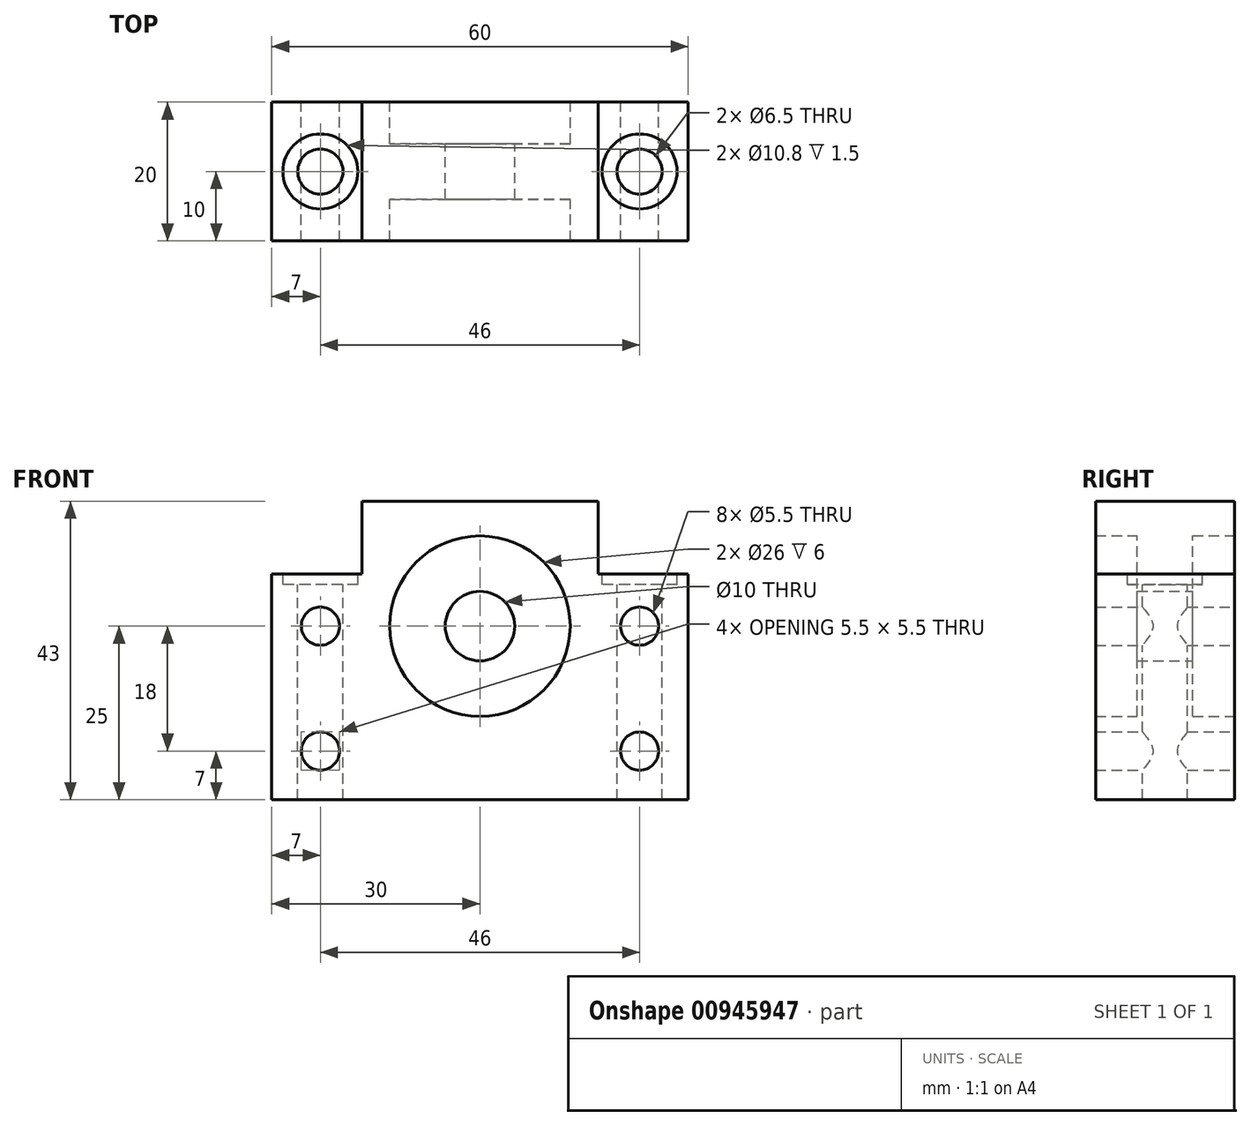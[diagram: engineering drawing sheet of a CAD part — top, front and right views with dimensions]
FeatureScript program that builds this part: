
annotation { "Feature Type Name" : "Feature", "Feature Type Description" : "" }
export const myFeature = defineFeature(function(context is Context, id is Id, definition is map)
    precondition{}
    {
        {
            var Q0;
            Q0=qCreatedBy(makeId("Front.planeOp"),FACE);
            var sketch = newSketch(context, id + "F0", { "sketchPlane" : qUnion([Q0])});
            skLineSegment(sketch, "E0.bottom", {"start": v(30, -16.25) * mm, "end": v(-30, -16.25) * mm});
            skLineSegment(sketch, "E0.top", {"start": v(30, 16.25) * mm, "end": v(17, 16.25) * mm});
            skLineSegment(sketch, "E0.left", {"start": v(30, -16.25) * mm, "end": v(30, 16.25) * mm});
            skLineSegment(sketch, "E0.right", {"start": v(-30, -16.25) * mm, "end": v(-30, 16.25) * mm});
            skPoint(sketch, "E0.middle", {"position": v(0, 0) * mm});
            skLineSegment(sketch, "E1.top", {"start": v(17, 26.75) * mm, "end": v(-17, 26.75) * mm});
            skLineSegment(sketch, "E1.left", {"start": v(17, 16.25) * mm, "end": v(17, 26.75) * mm});
            skLineSegment(sketch, "E1.right", {"start": v(-17, 16.25) * mm, "end": v(-17, 26.75) * mm});
            skPoint(sketch, "E1.middle", {"position": v(0, 21.5) * mm});
            skLineSegment(sketch, "E2.trimOffspring", {"start": v(-17, 16.25) * mm, "end": v(-30, 16.25) * mm});
            skCircle(sketch, "E3", {"center": v(0, 8.75) * mm, "radius": 13 * mm});
            skCircle(sketch, "E4", {"center": v(-23, 8.75) * mm, "radius": 2.75 * mm});
            skCircle(sketch, "E5", {"center": v(-23, -9.25) * mm, "radius": 2.75 * mm});
            skLineSegment(sketch, "E6", {"start": v(0, 26.75) * mm, "end": v(0, -16.25) * mm, "construction": true});
            skCircle(sketch, "E7.MirrorC", {"center": v(23, -9.25) * mm, "radius": 2.75 * mm});
            skCircle(sketch, "E8.MirrorC", {"center": v(23, 8.75) * mm, "radius": 2.75 * mm});
            skSolve(sketch);
        }
        {
            var Q0;
            Q0 = qSketchRegion(id + "F0", true);
            extrude(context, id + "F1", {"entities" : qUnion([Q0]), "depth" : 10 * mm, "offsetDistance" : 25 * mm, "hasSecondDirection" : true, "secondDirectionOppositeDirection" : true, "secondDirectionDepth" : 10 * mm});
        }
        {
            var Q0;
            Q0=qCreatedBy(makeId("Front.planeOp"),FACE);
            var sketch = newSketch(context, id + "F2", { "sketchPlane" : qUnion([Q0])});
            skCircle(sketch, "E9.0", {"center": v(0, 8.75) * mm, "radius": 13 * mm});
            skCircle(sketch, "E10", {"center": v(0, 8.75) * mm, "radius": 5 * mm});
            skSolve(sketch);
        }
        {
            var Q0;
            Q0 = qSketchRegion(id + "F2", true);
            extrude(context, id + "F3", {"entities" : qUnion([Q0]), "operationType" : NewBodyOperationType.ADD, "depth" : 4 * mm, "offsetDistance" : 25 * mm, "hasSecondDirection" : true, "secondDirectionOppositeDirection" : true, "secondDirectionDepth" : 4 * mm});
        }
        {
            var Q0;
            Q0=makeQuery(id+"F1.opExtrude","SWEPT_FACE",FACE,{"disambiguationData":[OSD([sQuery(id+"F0.wireOp",EDGE,"E2.trimOffspring")])]});
            var sketch = newSketch(context, id + "F4", { "sketchPlane" : qUnion([Q0])});
            skCircle(sketch, "E11", {"center": v(-23, 0) * mm, "radius": 3.25 * mm});
            skLineSegment(sketch, "E12", {"start": v(0, -3.38) * mm, "end": v(0, -20.15) * mm, "construction": true});
            skCircle(sketch, "E13.MirrorC", {"center": v(23, 0) * mm, "radius": 3.25 * mm});
            skSolve(sketch);
        }
        {
            var Q0;
            Q0 = qSketchRegion(id + "F4", true);
            extrude(context, id + "F5", {"entities" : qUnion([Q0]), "operationType" : NewBodyOperationType.REMOVE, "endBound" : BoundingType.THROUGH_ALL, "oppositeDirection" : true, "depth" : 25 * mm, "offsetDistance" : 25 * mm});
        }
        {
            var Q0;
            Q0=makeQuery(id+"F1.opExtrude","SWEPT_FACE",FACE,{"disambiguationData":[OSD([sQuery(id+"F0.wireOp",EDGE,"E2.trimOffspring")])]});
            var sketch = newSketch(context, id + "F6", { "sketchPlane" : qUnion([Q0])});
            skCircle(sketch, "E14", {"center": v(-23, 0) * mm, "radius": 5.4 * mm});
            skLineSegment(sketch, "E15", {"start": v(0, -1.93) * mm, "end": v(0, -15.4) * mm, "construction": true});
            skCircle(sketch, "E16.MirrorC", {"center": v(23, 0) * mm, "radius": 5.4 * mm});
            skSolve(sketch);
        }
        {
            var Q0;
            Q0 = qSketchRegion(id + "F6", true);
            extrude(context, id + "F7", {"entities" : qUnion([Q0]), "operationType" : NewBodyOperationType.REMOVE, "oppositeDirection" : true, "depth" : 1.5 * mm, "offsetDistance" : 25 * mm});
        }
    });
